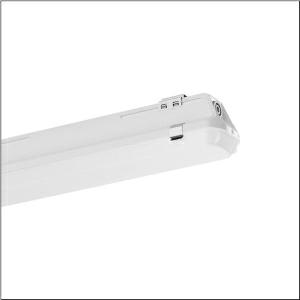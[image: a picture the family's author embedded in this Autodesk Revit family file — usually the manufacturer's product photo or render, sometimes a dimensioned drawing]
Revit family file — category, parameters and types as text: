
# Revit family: monsun_r__11_51fp20ep460h_939a
name_source: partatom
category: Lighting Fixtures
units: mm (PartAtom-declared; Revit-internal decimal feet)

## family parameters
Cut with Voids When Loaded = No
Host = Face
Light Source = No
Part Type = Normal
Room Calculation Point = No
Round Connector Dimension = Use Diameter
Shared = No

## types (1)
- --- (1 x LED, 5450 lm, 34.6 W, 4000K)
    Apparent Load = 35 VA
    CIE Flux Codes = 45 75 93 94 100
    Color Rendering = 80
    Color Temperature = 4000K
    Default Elevation = 1800 mm
    Description = Monsun® 11, damp-proof luminaire, chain hanger, primary optical cover: enclosure, of PC, light emission: direct distribution, primary light characteristic: symmetric, installation type: suspended mounting, surface-mounted, horizontal mounting, vertical mounting, LED, rated luminous flux: 5.450lm, luminous efficacy: 158lm/W, light colour: 840, colour temperature: 4000K, control gear: ECG DALI, with terminal, 5-pole, max. 2.5mm², mains connection: 220..240V, AC, 50/60Hz, rated input power: 35W, luminaire housing, of glass-fibre reinforced polyester, uncoated, bright grey, incl. chain hanger, length: 1.590mm, width: 90mm, height: 88mm, clip for enclosure, of stainless steel (V2A), ceiling mounting element, of stainless steel (V2A), chain hanger, of stainless steel (V2A), protection rating (complete): IP66, insulation class (complete): insulation class I (protective earthing), certification: CE, ENEC, VDE, UKCA, protection symbol: D, impact resistance: IK08, permissible operating ambient temperature: -25..+40°C, standard: EN 50419, EN 60598-2-1, no direct snow, no direct sun, no direct rain, for indoor or canopied outdoor use, corresponds to IFS (International Featured Standards) requirements for safety and quality in the food industry, contact your sales advisor before using the luminaires in applications with unclear chemical exposure, large temperature fluctuations or condensation-forming humidity, LABS conformity tested according to VDMA 24364:2018-05, packaging unit: 1 piece
    Height = 89 mm
    Lamp = 1 x LED
    Lamp Light Flux = 5450 lm
    Lamp Power = 34.6 W
    Lamp count = 1
    Length = 1590 mm
    Luminous efficacy = 158 lm/W
    Manufacturer = Siteco
    ModVariant = No
    Model = 51FP20EP460H
    Mounting Place = Ceiling
    Mounting Type = Surface mounted
    Number of Poles = 1
    OnlyDefault = Yes
    Power Factor = 1
    Product Name = Monsun® 11
    Product group = damp-proof luminaire
    ProductGroupID = 300
    Protection Class = Protection class I
    Protection Degree = IP 66
    RLX_Detail_Level = 1
    RLX_Emergency_Light_Flux = 0 lm
    RLX_Emergency_Type = 0
    RLX_Emergency_Type_DB = No
    RlxData = <blob elided: 92153 chars, md5=aabeb0ac>
    Socket = socket
    Standby Power = 0 W
    System Light Flux = 5450 lm
    System Power = 35 W
    Type Comments = factory setting: luminous flux: 100 % | dim-lin: 254 | 232 mA
    Type Image = l_1319650.jpg
    URL = http://relux.com
    VarID = @adj_174061
    Voltage = 0 V
    Weight = 0.00 kg
    Width = 90 mm

## geometry (parser evidence)
native form markers: Blend x4, Sweep x14
no freeform markers — native parametric forms only
